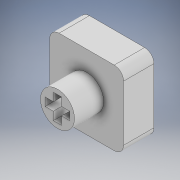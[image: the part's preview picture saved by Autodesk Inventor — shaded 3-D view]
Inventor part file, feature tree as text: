
AUTODESK INVENTOR PART (.ipt)
format: ipt  version: 2022 (Build 260153000, 153)  size: 248,320 bytes
history: native  units: in
note: dims shown in document units (in); Inventor stores cm internally (conversion verified against a paired STEP export)
features: sketch x4, extrude x3, plane x1, projected_geometry x1
ambient origin geometry x8: Origin, YZ Plane, XZ Plane, XY Plane, X Axis, Y Axis, Z Axis, Center Point
bodies: Body1 (feature_tree)
feature tree (9):
  sketch  "Sketch1"  dims[d3=0.2205in d4=0.1594in]
  plane  "Work Plane1"
  sketch  "Sketch2"  dims[d5=0.0531in d6=0.1594in]
  extrude  "Extrusion3"  Depth=0.1594in
  extrude  "Extrusion4"  Depth=0.1594in
  extrude  "Extrusion5"  Depth=0.5016in
  projected_geometry  "Projected Loop1"
  sketch  "Sketch3"  dims[d7=0.0531in d10=0.5016in]
  sketch  "Sketch4"  dims[d12=0.1969in d13=0.0in d14=0.2205in d15=0.1594in d16=0.0531in d17=0.1594in d18=0.0531in d19=0.189in d20=0.0in d21=0.0892in d22=0.2693in d23=0.0354in d24=0.0in]
